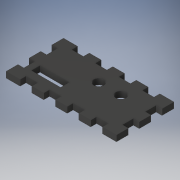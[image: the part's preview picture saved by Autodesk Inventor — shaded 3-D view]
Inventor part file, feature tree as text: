
AUTODESK INVENTOR PART (.ipt)
format: ipt  version: 2019 (Build 230136000, 136)  size: 188,928 bytes
history: native  units: mm
features: extrude x2, sketch x2
ambient origin geometry x8: Origin, YZ Plane, XZ Plane, XY Plane, X Axis, Y Axis, Z Axis, Center Point
bodies: Solid1 (feature_tree)
feature tree (4):
  extrude  "Extrusion1"  Depth=39.0mm
  extrude  "Extrusion2"  Depth=6.0mm
  sketch  "Sketch1"  dims[d0=75.0mm d1=39.0mm]
  sketch  "Sketch2"  dims[d2=20.0mm d3=6.0mm d4=9.0mm d5=8.0mm d6=7.0mm d7=25.0mm d8=38.0mm d9=15.0mm d10=4.0mm d11=0.0mm d12=4.0mm d13=4.0mm d14=8.0mm d15=8.0mm d16=8.0mm d17=8.0mm d18=4.0mm d19=4.0mm d20=0.0mm]
